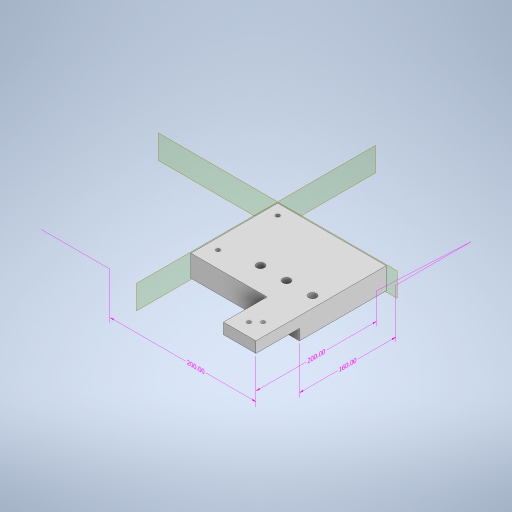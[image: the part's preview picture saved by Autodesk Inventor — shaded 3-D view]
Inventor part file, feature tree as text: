
AUTODESK INVENTOR PART (.ipt)
format: ipt  version: 2023 (Build 270158000, 158)  size: 375,296 bytes
history: native  units: mm
features: sketch x8, other x5, extrude x5, hole x3, plane x2, split x2
ambient origin geometry x8: Origin, YZ Plane, XZ Plane, XY Plane, X Axis, Y Axis, Z Axis, Center Point
bodies: Body1 (feature_tree)
feature tree (25):
  other  "Sólido1"
  other  "Anotaciones"
  extrude  "Extrusión1"  Depth=160.0mm
  extrude  "Extrusión2"  TaperAngle=0.0deg  [1 undecoded]
  extrude  "Extrusión3"  Depth=20.0mm TaperAngle=0.0deg
  extrude  "Extrusión4"  Depth=10.0mm
  hole  "Agujero1"  [1 undecoded]
  plane  "Plano de trabajo1"
  plane  "Plano de trabajo2"
  hole  "Agujero2"  [1 undecoded]
  extrude  "Extrusión5"  Depth=10.0mm
  hole  "Agujero3"  [1 undecoded]
  split  "Dividir1"
  split  "Dividir2"
  sketch  "Boceto1"  dims[d0=200.0mm d1=160.0mm]
  sketch  "Boceto2"  dims[d2=20.0mm d3=0.0mm]
  sketch  "Boceto3"  dims[d4=7.0mm d5=68.0mm d6=80.0mm d7=7.6mm d8=10.0mm d9=7.0mm d10=24.0mm d11=10.0mm d16=0.0mm]
  sketch  "Boceto4"  dims[d19=40.0mm d20=20.0mm d21=0.0mm]
  sketch  "Boceto5"  dims[d22=30.0mm d23=10.0mm]
  sketch  "Boceto6"  dims[d24=40.0mm d25=0.0mm d26=1.75mm]
  sketch  "Boceto7"  dims[d27=8.25mm d28=20.0mm]
  sketch  "Boceto8"  dims[d29=10.0mm d30=10.0mm d31=1.75mm d32=1.75mm d33=1.75mm d34=40.0mm d35=0.0mm d36=11.749873mm d37=40.0mm d38=29.999873mm d39=21.75mm d40=11.75mm d41=28.300341mm d42=11.749873mm d43=0.0mm d44=0.0mm d45=3.5mm d46=6.0mm d47=4.0mm d48=2.0mm d49=90.0deg d50=8.0mm d51=20.594885mm d58=30.0mm d59=30.0mm d63=3.5mm d64=10.0mm d65=10.0mm d66=3.5mm d67=6.0mm d68=4.0mm d69=2.0mm d70=90.0deg d71=8.0mm d72=20.594885mm d73=32.0mm d74=32.0mm d75=10.0mm d76=0.0mm d77=10.0mm d78=30.0mm d79=5.0mm d80=5.0mm d81=5.0mm d82=5.0mm d83=3.5mm d84=6.0mm d85=4.0mm d86=2.0mm d87=90.0deg d88=8.0mm d89=20.594885mm d52=6.692993mm d53=5.009025mm d54=200.0mm d55=6.065637mm d56=3.288093mm d57=200.0mm d60=3.204885mm d61=4.144173mm d62=160.0mm]
  other  "Cota lineal 1"
  other  "Cota lineal 2"
  other  "Cota lineal 3"
note: 4 required parameter values undecoded (feature->parameter linkage not recoverable at this tier; creation-order binding heuristic only, values carry confidence <= 0.55)
